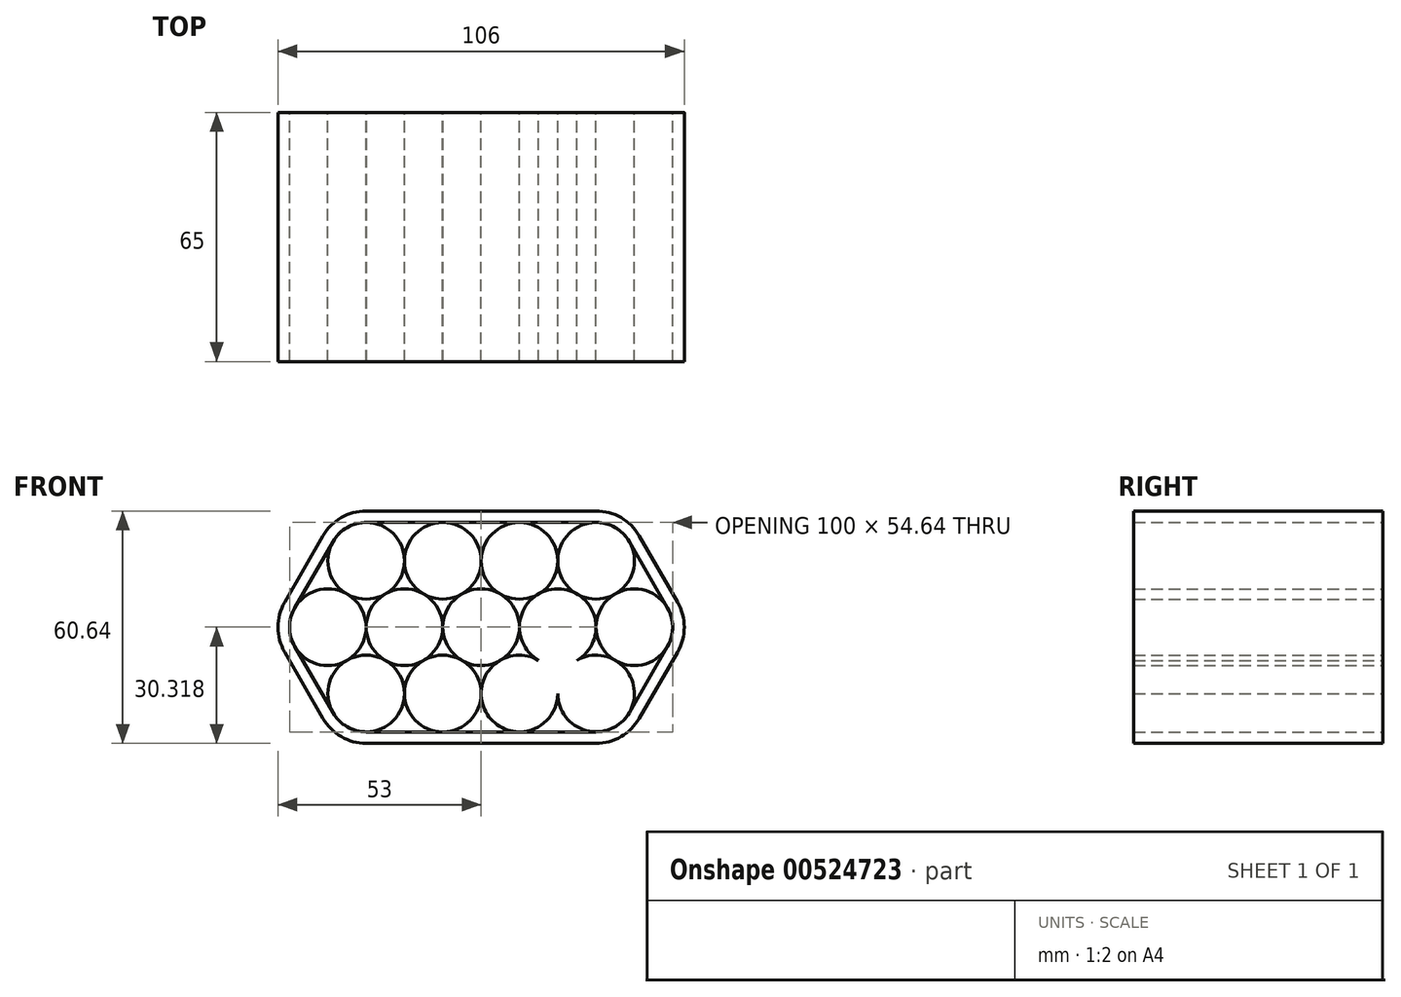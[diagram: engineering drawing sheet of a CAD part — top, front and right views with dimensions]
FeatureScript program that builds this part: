
annotation { "Feature Type Name" : "Feature", "Feature Type Description" : "" }
export const myFeature = defineFeature(function(context is Context, id is Id, definition is map)
    precondition{}
    {
        {
            var Q0;
            Q0=qCreatedBy(makeId("Front.planeOp"),FACE);
            var sketch = newSketch(context, id + "F0", { "sketchPlane" : qUnion([Q0])});
            skCircle(sketch, "E0", {"center": v(-49.42, 44.86) * mm, "radius": 10 * mm});
            skCircle(sketch, "E1.1.0.0", {"center": v(-29.42, 44.86) * mm, "radius": 10 * mm});
            skCircle(sketch, "E1.2.0.0", {"center": v(-9.42, 44.86) * mm, "radius": 10 * mm});
            skCircle(sketch, "E1.3.0.0", {"center": v(10.58, 44.86) * mm, "radius": 10 * mm});
            skLineSegment(sketch, "E1.direction1", {"start": v(-49.42, 44.86) * mm, "end": v(-29.42, 44.86) * mm, "construction": true});
            skCircle(sketch, "E2", {"center": v(-39.42, 27.54) * mm, "radius": 10 * mm});
            skCircle(sketch, "E3.1.0.0", {"center": v(-19.42, 27.54) * mm, "radius": 10 * mm});
            skCircle(sketch, "E3.2.0.0", {"center": v(0.58, 27.54) * mm, "radius": 10 * mm});
            skLineSegment(sketch, "E3.direction1", {"start": v(-39.42, 27.54) * mm, "end": v(-19.42, 27.54) * mm, "construction": true});
            skCircle(sketch, "E4", {"center": v(-39.42, 62.18) * mm, "radius": 10 * mm});
            skCircle(sketch, "E5.1.0.0", {"center": v(-19.42, 62.18) * mm, "radius": 10 * mm});
            skCircle(sketch, "E5.2.0.0", {"center": v(0.58, 62.18) * mm, "radius": 10 * mm});
            skLineSegment(sketch, "E5.direction1", {"start": v(-39.42, 62.18) * mm, "end": v(-19.42, 62.18) * mm, "construction": true});
            skCircle(sketch, "E6.0.3.0", {"center": v(20.58, 62.18) * mm, "radius": 10 * mm});
            skCircle(sketch, "E7.0.4.0", {"center": v(30.58, 44.86) * mm, "radius": 10 * mm});
            skCircle(sketch, "E8.0.3.0", {"center": v(20.58, 27.54) * mm, "radius": 10 * mm});
            skLineSegment(sketch, "E9", {"start": v(-39.3, 72.18) * mm, "end": v(20.58, 72.18) * mm});
            skLineSegment(sketch, "E10", {"start": v(-49.42, 44.86) * mm, "end": v(30.58, 44.86) * mm, "construction": true});
            skLineSegment(sketch, "E11", {"start": v(-48.08, 67.18) * mm, "end": v(-58.08, 49.86) * mm});
            skLineSegment(sketch, "E12", {"start": v(29.24, 67.18) * mm, "end": v(39.24, 49.86) * mm});
            skLineSegment(sketch, "E13.MirrorCS", {"start": v(29.24, 22.54) * mm, "end": v(39.24, 39.86) * mm});
            skLineSegment(sketch, "E14.MirrorCS", {"start": v(-48.08, 22.54) * mm, "end": v(-58.08, 39.86) * mm});
            skLineSegment(sketch, "E15.MirrorCS", {"start": v(-39.3, 17.54) * mm, "end": v(20.58, 17.54) * mm});
            skLineSegment(sketch, "E16.0", {"start": v(-39.42, 75.18) * mm, "end": v(20.58, 75.18) * mm});
            skLineSegment(sketch, "E17.0", {"start": v(-50.68, 68.68) * mm, "end": v(-60.68, 51.36) * mm});
            skLineSegment(sketch, "E18.0", {"start": v(31.84, 68.68) * mm, "end": v(41.84, 51.36) * mm});
            skLineSegment(sketch, "E19.MirrorCS", {"start": v(31.84, 21.04) * mm, "end": v(41.84, 38.36) * mm});
            skLineSegment(sketch, "E20.MirrorCS", {"start": v(-50.68, 21.04) * mm, "end": v(-60.68, 38.36) * mm});
            skLineSegment(sketch, "E21.MirrorCS", {"start": v(-39.42, 14.54) * mm, "end": v(20.58, 14.54) * mm});
            skPoint(sketch, "E22.newPointA", {"position": v(41.84, 51.36) * mm});
            skPoint(sketch, "E22.newPointB", {"position": v(41.84, 38.36) * mm});
            skArc(sketch, "E22.filletArc", {"start": v(41.84, 38.36) * mm, "mid": v(43.58, 44.86) * mm, "end": v(41.84, 51.36) * mm});
            skPoint(sketch, "E23.newPointA", {"position": v(-60.68, 38.36) * mm});
            skPoint(sketch, "E23.newPointB", {"position": v(-60.68, 51.36) * mm});
            skArc(sketch, "E23.filletArc", {"start": v(-60.68, 51.36) * mm, "mid": v(-62.42, 44.86) * mm, "end": v(-60.68, 38.36) * mm});
            skPoint(sketch, "E24.orphan", {"position": v(20.58, 75.18) * mm});
            skPoint(sketch, "E25.orphan", {"position": v(31.84, 68.68) * mm});
            skPoint(sketch, "E26.visualSharp", {"position": v(28.09, 75.18) * mm});
            skArc(sketch, "E26.filletArc", {"start": v(31.84, 68.68) * mm, "mid": v(27.08, 73.44) * mm, "end": v(20.58, 75.18) * mm});
            skPoint(sketch, "E27.newPointA", {"position": v(31.84, 21.04) * mm});
            skPoint(sketch, "E27.newPointB", {"position": v(20.58, 14.54) * mm});
            skArc(sketch, "E27.filletArc", {"start": v(20.58, 14.54) * mm, "mid": v(27.08, 16.28) * mm, "end": v(31.84, 21.04) * mm});
            skPoint(sketch, "E28.orphan", {"position": v(-50.68, 68.68) * mm});
            skPoint(sketch, "E29.orphan", {"position": v(-39.3, 75.18) * mm});
            skPoint(sketch, "E30.visualSharp", {"position": v(-46.93, 75.18) * mm});
            skArc(sketch, "E30.filletArc", {"start": v(-39.42, 75.18) * mm, "mid": v(-45.92, 73.44) * mm, "end": v(-50.68, 68.68) * mm});
            skPoint(sketch, "E31.orphan", {"position": v(-50.68, 21.04) * mm});
            skPoint(sketch, "E32.orphan", {"position": v(-39.3, 14.54) * mm});
            skPoint(sketch, "E33.visualSharp", {"position": v(-46.93, 14.54) * mm});
            skArc(sketch, "E33.filletArc", {"start": v(-50.68, 21.04) * mm, "mid": v(-45.92, 16.28) * mm, "end": v(-39.42, 14.54) * mm});
            skSolve(sketch);
        }
        {
            var Q0;
            {var subQ0=sQuery(id+"F0.wireOp",EDGE,"E6.0.3.0");var subQ1=makeQuery(id+"F0.imprint","INTERSECT",VERTEX,{"derivedFrom":[sQuery(id+"F0.wireOp",EDGE,"E5.2.0.0"),subQ0]});Q0=makeQuery(id+"F0.imprint","IMPRINT",FACE,{"disambiguationData":[TD([[makeQuery(id+"F0.imprint","IMPRINT",EDGE,{"disambiguationData":[TD([[subQ1,-1.0]])],"derivedFrom":subQ0}),1.0]])]});}
            var Q1;
            {var subQ0=sQuery(id+"F0.wireOp",EDGE,"E7.0.4.0");var subQ1=makeQuery(id+"F0.imprint","INTERSECT",VERTEX,{"derivedFrom":[sQuery(id+"F0.wireOp",EDGE,"E6.0.3.0"),subQ0]});Q1=makeQuery(id+"F0.imprint","IMPRINT",FACE,{"disambiguationData":[TD([[makeQuery(id+"F0.imprint","IMPRINT",EDGE,{"disambiguationData":[TD([[subQ1,-1.0]])],"derivedFrom":subQ0}),1.0]])]});}
            var Q2;
            {var subQ0=sQuery(id+"F0.wireOp",EDGE,"E8.0.3.0");var subQ1=makeQuery(id+"F0.imprint","INTERSECT",VERTEX,{"derivedFrom":[sQuery(id+"F0.wireOp",EDGE,"E7.0.4.0"),subQ0]});Q2=makeQuery(id+"F0.imprint","IMPRINT",FACE,{"disambiguationData":[TD([[makeQuery(id+"F0.imprint","IMPRINT",EDGE,{"disambiguationData":[TD([[subQ1,-1.0]])],"derivedFrom":subQ0}),1.0]])]});}
            var Q3;
            {var subQ0=sQuery(id+"F0.wireOp",EDGE,"E5.2.0.0");var subQ1=makeQuery(id+"F0.imprint","INTERSECT",VERTEX,{"derivedFrom":[sQuery(id+"F0.wireOp",EDGE,"E5.1.0.0"),subQ0]});Q3=makeQuery(id+"F0.imprint","IMPRINT",FACE,{"disambiguationData":[TD([[makeQuery(id+"F0.imprint","IMPRINT",EDGE,{"disambiguationData":[TD([[subQ1,1.0]])],"derivedFrom":subQ0}),1.0]])]});}
            var Q4;
            {var subQ0=sQuery(id+"F0.wireOp",EDGE,"E1.3.0.0");var subQ4=makeQuery(id+"F0.imprint","INTERSECT",VERTEX,{"derivedFrom":[subQ0,sQuery(id+"F0.wireOp",EDGE,"E6.0.3.0")]});Q4=makeQuery(id+"F0.imprint","IMPRINT",FACE,{"disambiguationData":[TD([[makeQuery(id+"F0.imprint","IMPRINT",EDGE,{"disambiguationData":[TD([[subQ4,1.0]])],"derivedFrom":subQ0}),1.0]])]});}
            var Q5;
            {var subQ0=sQuery(id+"F0.wireOp",EDGE,"E3.2.0.0");var subQ1=sQuery(id+"F0.wireOp",EDGE,"E1.3.0.0");var subQ2=makeQuery(id+"F0.imprint","INTERSECT",VERTEX,{"derivedFrom":[subQ1,subQ0]});Q5=makeQuery(id+"F0.imprint","IMPRINT",FACE,{"disambiguationData":[TD([[makeQuery(id+"F0.imprint","IMPRINT",EDGE,{"disambiguationData":[TD([[subQ2,-1.0]])],"derivedFrom":subQ1}),-1.0]])]});}
            var Q6;
            {var subQ0=sQuery(id+"F0.wireOp",EDGE,"E1.2.0.0");var subQ4=makeQuery(id+"F0.imprint","INTERSECT",VERTEX,{"derivedFrom":[subQ0,sQuery(id+"F0.wireOp",EDGE,"E5.2.0.0")]});Q6=makeQuery(id+"F0.imprint","IMPRINT",FACE,{"disambiguationData":[TD([[makeQuery(id+"F0.imprint","IMPRINT",EDGE,{"disambiguationData":[TD([[subQ4,1.0]])],"derivedFrom":subQ0}),1.0]])]});}
            var Q7;
            {var subQ0=sQuery(id+"F0.wireOp",EDGE,"E5.1.0.0");var subQ1=makeQuery(id+"F0.imprint","INTERSECT",VERTEX,{"derivedFrom":[sQuery(id+"F0.wireOp",EDGE,"E4"),subQ0]});Q7=makeQuery(id+"F0.imprint","IMPRINT",FACE,{"disambiguationData":[TD([[makeQuery(id+"F0.imprint","IMPRINT",EDGE,{"disambiguationData":[TD([[subQ1,1.0]])],"derivedFrom":subQ0}),1.0]])]});}
            var Q8;
            {var subQ0=sQuery(id+"F0.wireOp",EDGE,"E4");var subQ1=makeQuery(id+"F0.imprint","INTERSECT",VERTEX,{"derivedFrom":[sQuery(id+"F0.wireOp",EDGE,"E0"),subQ0]});Q8=makeQuery(id+"F0.imprint","IMPRINT",FACE,{"disambiguationData":[TD([[makeQuery(id+"F0.imprint","IMPRINT",EDGE,{"disambiguationData":[TD([[subQ1,1.0]])],"derivedFrom":subQ0}),1.0]])]});}
            var Q9;
            {var subQ0=sQuery(id+"F0.wireOp",EDGE,"E1.1.0.0");var subQ4=makeQuery(id+"F0.imprint","INTERSECT",VERTEX,{"derivedFrom":[subQ0,sQuery(id+"F0.wireOp",EDGE,"E5.1.0.0")]});Q9=makeQuery(id+"F0.imprint","IMPRINT",FACE,{"disambiguationData":[TD([[makeQuery(id+"F0.imprint","IMPRINT",EDGE,{"disambiguationData":[TD([[subQ4,1.0]])],"derivedFrom":subQ0}),1.0]])]});}
            var Q10;
            {var subQ0=sQuery(id+"F0.wireOp",EDGE,"E3.2.0.0");var subQ1=makeQuery(id+"F0.imprint","INTERSECT",VERTEX,{"derivedFrom":[subQ0,sQuery(id+"F0.wireOp",EDGE,"E8.0.3.0")]});Q10=makeQuery(id+"F0.imprint","IMPRINT",FACE,{"disambiguationData":[TD([[makeQuery(id+"F0.imprint","IMPRINT",EDGE,{"disambiguationData":[TD([[subQ1,-1.0]])],"derivedFrom":subQ0}),1.0]])]});}
            var Q11;
            {var subQ0=sQuery(id+"F0.wireOp",EDGE,"E3.1.0.0");var subQ1=makeQuery(id+"F0.imprint","INTERSECT",VERTEX,{"derivedFrom":[subQ0,sQuery(id+"F0.wireOp",EDGE,"E3.2.0.0")]});Q11=makeQuery(id+"F0.imprint","IMPRINT",FACE,{"disambiguationData":[TD([[makeQuery(id+"F0.imprint","IMPRINT",EDGE,{"disambiguationData":[TD([[subQ1,-1.0]])],"derivedFrom":subQ0}),1.0]])]});}
            var Q12;
            {var subQ0=sQuery(id+"F0.wireOp",EDGE,"E2");var subQ1=makeQuery(id+"F0.imprint","INTERSECT",VERTEX,{"derivedFrom":[subQ0,sQuery(id+"F0.wireOp",EDGE,"E3.1.0.0")]});Q12=makeQuery(id+"F0.imprint","IMPRINT",FACE,{"disambiguationData":[TD([[makeQuery(id+"F0.imprint","IMPRINT",EDGE,{"disambiguationData":[TD([[subQ1,-1.0]])],"derivedFrom":subQ0}),1.0]])]});}
            var Q13;
            {var subQ0=sQuery(id+"F0.wireOp",EDGE,"E0");var subQ1=makeQuery(id+"F0.imprint","INTERSECT",VERTEX,{"derivedFrom":[subQ0,sQuery(id+"F0.wireOp",EDGE,"E4")]});Q13=makeQuery(id+"F0.imprint","IMPRINT",FACE,{"disambiguationData":[TD([[makeQuery(id+"F0.imprint","IMPRINT",EDGE,{"disambiguationData":[TD([[subQ1,1.0]])],"derivedFrom":subQ0}),1.0]])]});}
            extrude(context, id + "F1", {"entities" : qUnion([Q0, Q1, Q2, Q3, Q4, Q5, Q6, Q7, Q8, Q9, Q10, Q11, Q12, Q13]), "depth" : 65 * mm, "offsetDistance" : 25 * mm});
        }
        {
            var Q0;
            {var subQ11=sQuery(id+"F0.wireOp",EDGE,"E11");Q0=makeQuery(id+"F0.imprint","IMPRINT",FACE,{"disambiguationData":[TD([[makeQuery(id+"F0.imprint","IMPRINT",EDGE,{"derivedFrom":subQ11}),-1.0]])]});}
            extrude(context, id + "F2", {"entities" : qUnion([Q0]), "depth" : 65 * mm, "offsetDistance" : 25 * mm});
        }
    });
